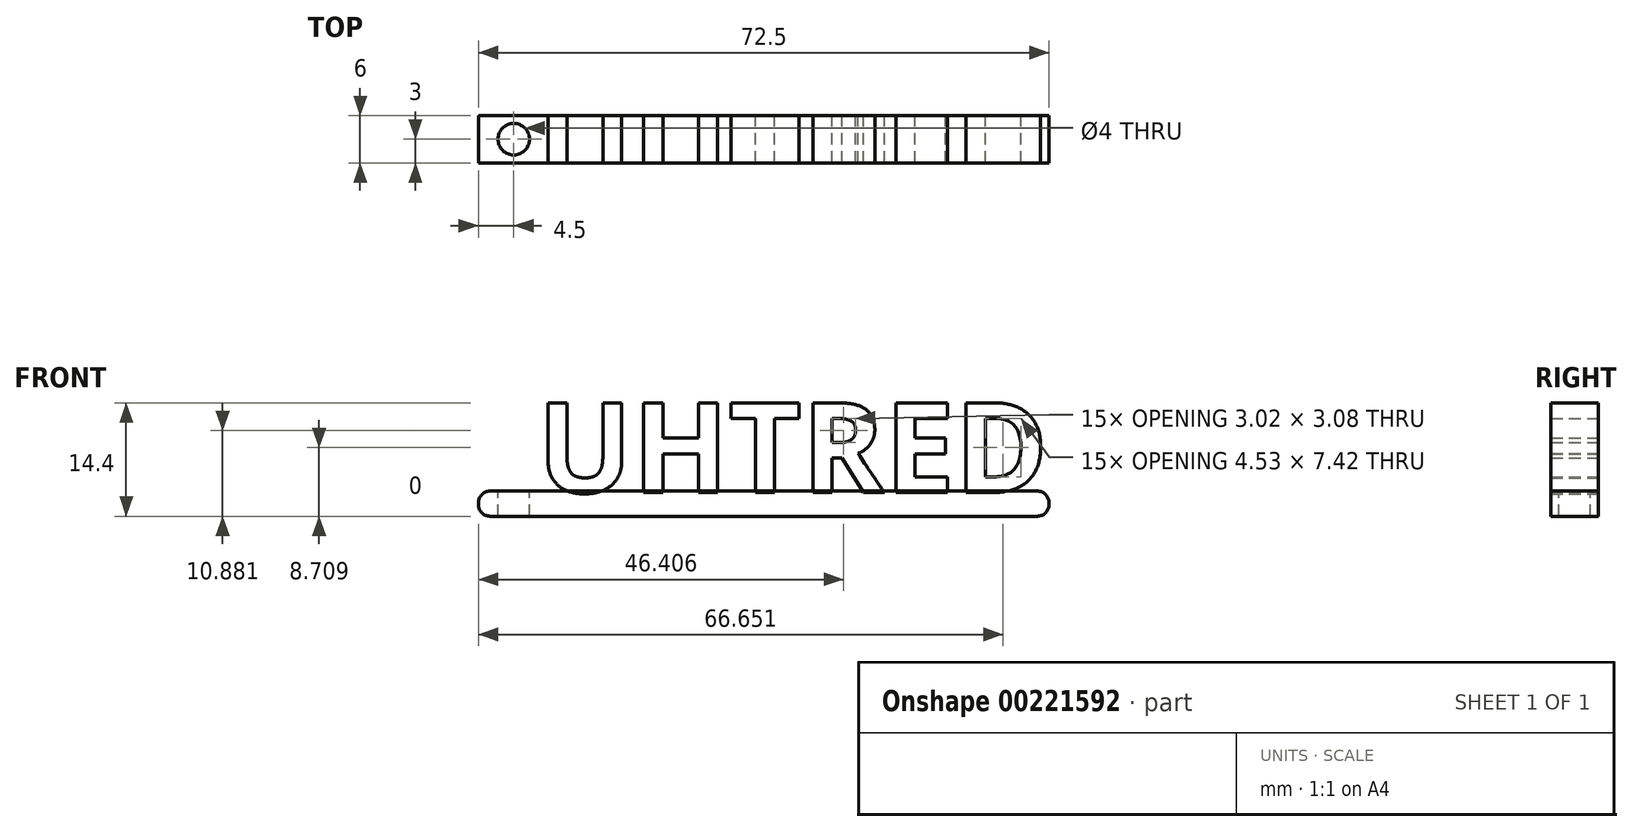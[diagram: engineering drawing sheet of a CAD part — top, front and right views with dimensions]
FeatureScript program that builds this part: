
annotation { "Feature Type Name" : "Feature", "Feature Type Description" : "" }
export const myFeature = defineFeature(function(context is Context, id is Id, definition is map)
    precondition{}
    {
        {
            var Q0;
            Q0=qCreatedBy(makeId("Front.planeOp"),FACE);
            var sketch = newSketch(context, id + "F0", { "sketchPlane" : qUnion([Q0])});
            skText(sketch, "E0", { "text": "UHTRED", "fontName": "OpenSans-Bold.ttf"});
            const initialGuessF0  = {"E0": [-0.02, 0, 1, 0, 0.0115]};
            skSetInitialGuess(sketch, initialGuessF0);
            skSolve(sketch);
        }
        {
            var Q0;
            Q0=qSketchRegion(id+"F0",true);
            extrude(context, id + "F1", {"entities" : qUnion([Q0]), "endBound" : BoundingType.SYMMETRIC, "depth" : 6 * mm});
        }
        {
            var Q0;
            Q0=qCreatedBy(makeId("Top.planeOp"),FACE);
            var sketch = newSketch(context, id + "F2", { "sketchPlane" : qUnion([Q0])});
            skLineSegment(sketch, "E1.bottom", {"start": v(-20, 3) * mm, "end": v(45, 3) * mm});
            skLineSegment(sketch, "E1.top", {"start": v(-20, -3) * mm, "end": v(45, -3) * mm});
            skLineSegment(sketch, "E1.left", {"start": v(-20, 3) * mm, "end": v(-20, -3) * mm});
            skLineSegment(sketch, "E1.right", {"start": v(45, 3) * mm, "end": v(45, -3) * mm});
            skSolve(sketch);
        }
        {
            var Q0;
            Q0=makeQuery(id+"F2.imprint","IMPRINT",FACE,{"disambiguationData":[TD([[makeQuery(id+"F2.imprint","IMPRINT",EDGE,{"derivedFrom":sQuery(id+"F2.wireOp",EDGE,"E1.bottom")}),-1.0]])]});
            extrude(context, id + "F3", {"entities" : qUnion([Q0]), "depth" : 0.2 * mm});
        }
        {
            var Q0;
            Q0=makeQuery(id+"F3.opExtrude","CAP_FACE",FACE,{"disambiguationData":[OSD([sQuery(id+"F2.wireOp",EDGE,"E1.bottom"),sQuery(id+"F2.wireOp",EDGE,"E1.top"),sQuery(id+"F2.wireOp",EDGE,"E1.left"),sQuery(id+"F2.wireOp",EDGE,"E1.right")])],"isStart":true});
            extrude(context, id + "F4", {"entities" : qUnion([Q0]), "depth" : 3 * mm});
        }
        {
            var Q0;
            {var subQ0=sQuery(id+"F2.wireOp",EDGE,"E1.left");Q0=makeQuery(id+"FaVoHrOpcFZXiYX_6.opBoolean","MERGE",FACE,{"derivedFrom":[makeQuery(id+"F3.opExtrude","SWEPT_FACE",FACE,{"disambiguationData":[OSD([subQ0])]}),makeQuery(id+"F4.opExtrude","SWEPT_FACE",FACE,{"disambiguationData":[OSD([subQ0])]})]});}
            var sketch = newSketch(context, id + "F5", { "sketchPlane" : qUnion([Q0])});
            skLineSegment(sketch, "E2.bottom", {"start": v(-3, -3) * mm, "end": v(3, -3) * mm});
            skLineSegment(sketch, "E2.top", {"start": v(-3, 0.2) * mm, "end": v(3, 0.2) * mm});
            skLineSegment(sketch, "E2.left", {"start": v(-3, -3) * mm, "end": v(-3, 0.2) * mm});
            skLineSegment(sketch, "E2.right", {"start": v(3, -3) * mm, "end": v(3, 0.2) * mm});
            skSolve(sketch);
        }
        {
            var Q0;
            Q0=qSketchRegion(id+"F5",true);
            extrude(context, id + "F6", {"entities" : qUnion([Q0]), "operationType" : NewBodyOperationType.ADD, "depth" : 7.5 * mm});
        }
        {
            var Q0;
            Q0=makeQuery(id+"F6.opExtrude","CAP_EDGE",EDGE,{"disambiguationData":[OSD([sQuery(id+"F5.wireOp",EDGE,"E2.bottom")])],"isStart":false});
            var Q1;
            Q1=makeQuery(id+"F6.opExtrude","CAP_EDGE",EDGE,{"disambiguationData":[OSD([sQuery(id+"F5.wireOp",EDGE,"E2.top")])],"isStart":false});
            var Q2;
            Q2=makeQuery(id+"F4.opExtrude","CAP_EDGE",EDGE,{"disambiguationData":[OSD([sQuery(id+"F2.wireOp",EDGE,"E1.right")])],"isStart":false});
            fillet(context, id + "F7", {"entities" : qUnion([Q0, Q1, Q2]), "radius" : 1.5 * mm, "tangentPropagation" : true, "allowEdgeOverflow" : false});
        }
        {
            var Q0;
            {var subQ19=sQuery(id+"F2.wireOp",EDGE,"E1.top");var subQ20=sQuery(id+"F2.wireOp",EDGE,"E1.bottom");var subQ63=sQuery(id+"F0.wireOp",EDGE,"E0.sketch_text.stroke-2");var subQ66=sQuery(id+"F2.wireOp",EDGE,"E1.left");Q0=makeQuery(id+"F6.boolean.opBoolean","MERGE",FACE,{"derivedFrom":[makeQuery(id+"FaVoHrOpcFZXiYX_6.opBoolean","SPLIT",FACE,{"disambiguationData":[TD([makeQuery(id+"F1.opExtrude","SWEPT_FACE",FACE,{"disambiguationData":[OSD([subQ63])]})])],"derivedFrom":makeQuery(id+"F3.opExtrude","CAP_FACE",FACE,{"disambiguationData":[OSD([subQ20,subQ19,subQ66,sQuery(id+"F2.wireOp",EDGE,"E1.right")])],"isStart":false})}),makeQuery(id+"F6.opExtrude","SWEPT_FACE",FACE,{"disambiguationData":[OSD([sQuery(id+"F5.wireOp",EDGE,"E2.top")])]})]});}
            var sketch = newSketch(context, id + "F8", { "sketchPlane" : qUnion([Q0])});
            skCircle(sketch, "E3", {"center": v(-23, 0) * mm, "radius": 2 * mm});
            skSolve(sketch);
        }
        {
            var Q0;
            Q0=makeQuery(id+"F8.imprint","IMPRINT",FACE,{"disambiguationData":[TD([[makeQuery(id+"F8.imprint","IMPRINT",EDGE,{"derivedFrom":sQuery(id+"F8.wireOp",EDGE,"E3")}),1.0]])]});
            extrude(context, id + "F9", {"entities" : qUnion([Q0]), "operationType" : NewBodyOperationType.REMOVE, "oppositeDirection" : true, "depth" : 3.5 * mm});
        }
        {
            var Q0;
            Q0=makeQuery(id+"F3.opExtrude","CAP_EDGE",EDGE,{"disambiguationData":[OSD([sQuery(id+"F2.wireOp",EDGE,"E1.right")])],"isStart":false});
            fillet(context, id + "F10", {"entities" : qUnion([Q0]), "radius" : 1.5 * mm, "tangentPropagation" : true, "allowEdgeOverflow" : false});
        }
    });
